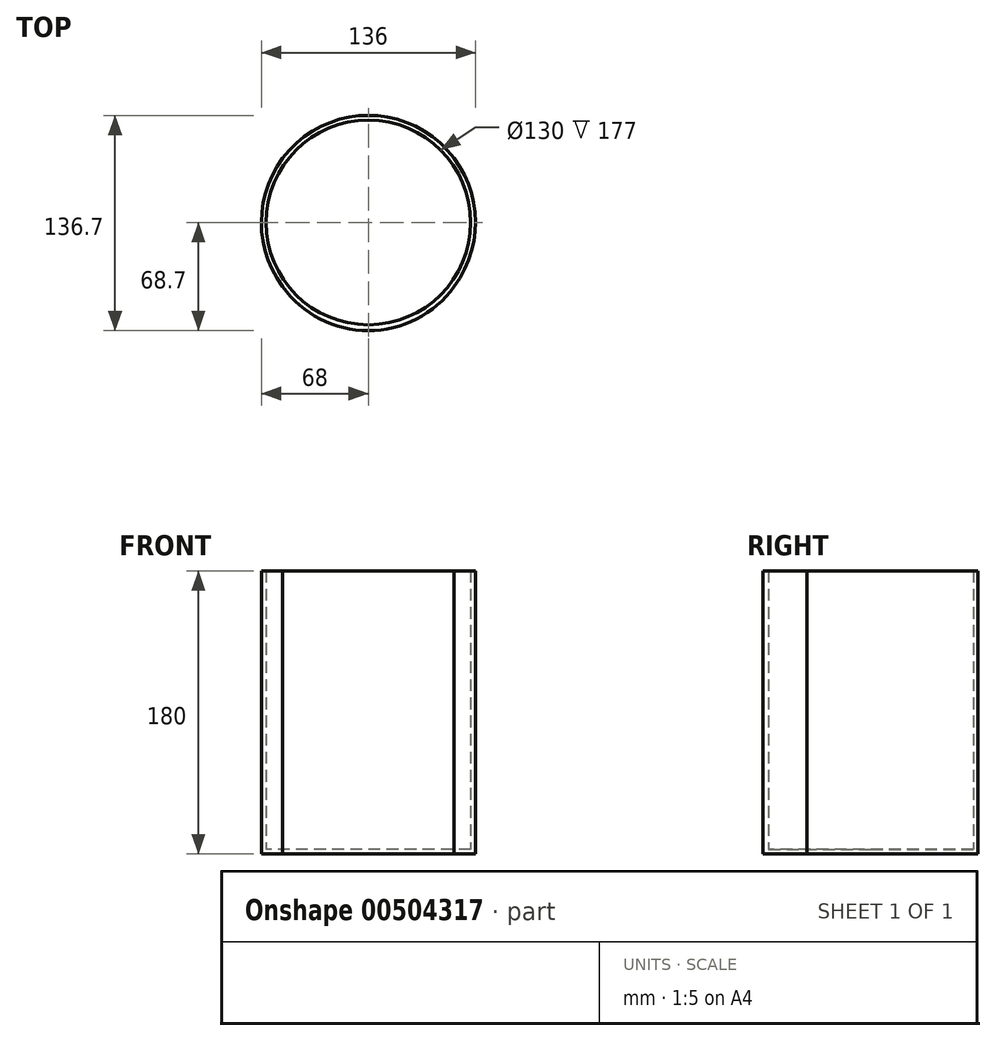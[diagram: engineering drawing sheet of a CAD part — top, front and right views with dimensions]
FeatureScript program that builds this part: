
annotation { "Feature Type Name" : "Feature", "Feature Type Description" : "" }
export const myFeature = defineFeature(function(context is Context, id is Id, definition is map)
    precondition{}
    {
        {
            var Q0;
            Q0=qCreatedBy(makeId("Top.planeOp"),FACE);
            var sketch = newSketch(context, id + "F0", { "sketchPlane" : qUnion([Q0])});
            skLineSegment(sketch, "E0", {"start": v(0, 0) * mm, "end": v(-65, 0) * mm});
            skLineSegment(sketch, "E1", {"start": v(-65, 0) * mm, "end": v(-68, 0) * mm});
            skCircle(sketch, "E2", {"center": v(0, 0) * mm, "radius": 65 * mm});
            skCircle(sketch, "E3", {"center": v(0, 0) * mm, "radius": 68 * mm});
            skCircle(sketch, "E4", {"center": v(0, -1.7) * mm, "radius": 67 * mm});
            skSolve(sketch);
        }
        {
            var Q0;
            Q0 = qSketchRegion(id + "F0", true);
            var Q1;
            Q1=makeQuery(id+"F0.imprint","IMPRINT",FACE,{"disambiguationData":[TD([[makeQuery(id+"F0.imprint","IMPRINT",EDGE,{"derivedFrom":sQuery(id+"F0.wireOp",EDGE,"E2")}),-1.0]])]});
            extrude(context, id + "F1", {"entities" : qUnion([Q0, Q1]), "depth" : 180 * mm});
        }
        {
            var Q0;
            Q0=makeQuery(id+"F0.imprint","IMPRINT",FACE,{"disambiguationData":[TD([[makeQuery(id+"F0.imprint","IMPRINT",EDGE,{"derivedFrom":sQuery(id+"F0.wireOp",EDGE,"E2")}),1.0]])]});
            extrude(context, id + "F2", {"entities" : qUnion([Q0]), "operationType" : NewBodyOperationType.ADD, "depth" : 3 * mm});
        }
    });
